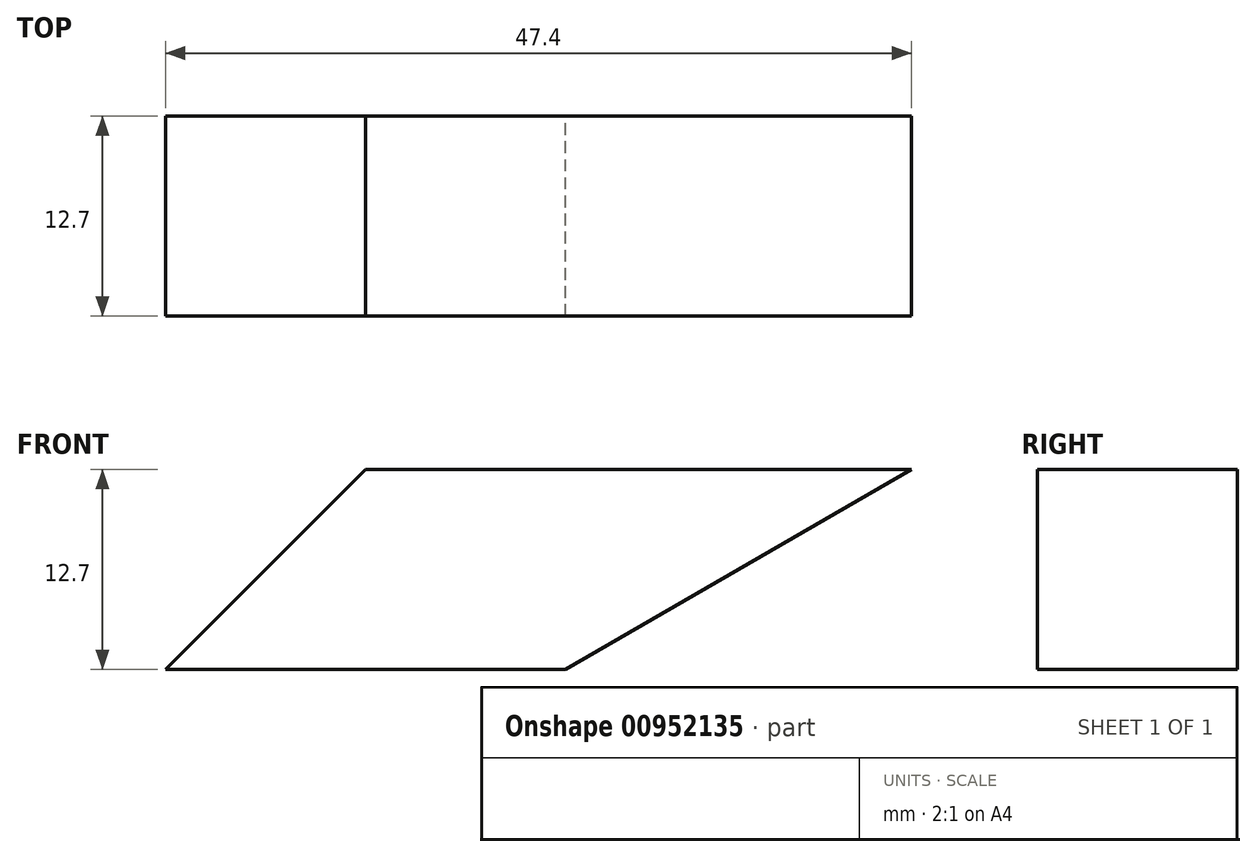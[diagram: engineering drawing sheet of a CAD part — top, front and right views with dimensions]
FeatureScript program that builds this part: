
annotation { "Feature Type Name" : "Feature", "Feature Type Description" : "" }
export const myFeature = defineFeature(function(context is Context, id is Id, definition is map)
    precondition{}
    {
        {
            var Q0;
            Q0=qCreatedBy(makeId("Front.planeOp"),FACE);
            var sketch = newSketch(context, id + "F0", { "sketchPlane" : qUnion([Q0])});
            skLineSegment(sketch, "E0", {"start": v(0, 0) * mm, "end": v(12.7, 12.7) * mm});
            skLineSegment(sketch, "E1", {"start": v(12.7, 12.7) * mm, "end": v(47.4, 12.7) * mm});
            skLineSegment(sketch, "E2", {"start": v(47.4, 12.7) * mm, "end": v(25.4, 0) * mm});
            skLineSegment(sketch, "E3", {"start": v(25.4, 0) * mm, "end": v(0, 0) * mm});
            skSolve(sketch);
        }
        {
            var Q0;
            Q0 = qSketchRegion(id + "F0", true);
            extrude(context, id + "F1", {"entities" : qUnion([Q0]), "depth" : 12.7 * mm, "offsetDistance" : 25.4 * mm});
        }
    });
